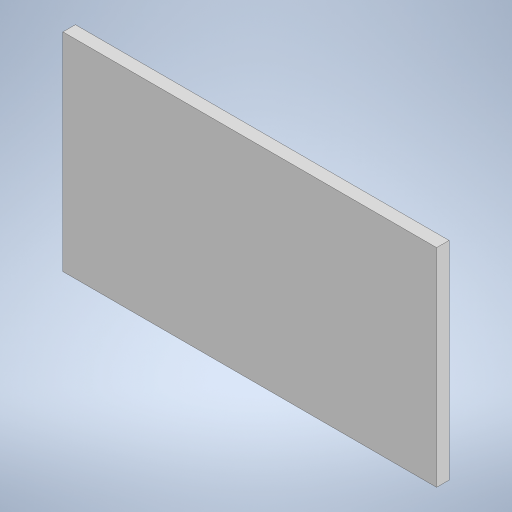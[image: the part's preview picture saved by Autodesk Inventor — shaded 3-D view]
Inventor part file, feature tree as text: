
AUTODESK INVENTOR PART (.ipt)
format: ipt  version: 2023 (Build 270158000, 158)  size: 182,784 bytes
history: native  units: mm
features: other x1, extrude x1, sketch x1
ambient origin geometry x8: Origin, YZ Plane, XZ Plane, XY Plane, X Axis, Y Axis, Z Axis, Center Point
bodies: Body1 (feature_tree)
feature tree (3):
  other  "ソリッド1"
  extrude  "押し出し1"  Depth=90.0mm
  sketch  "スケッチ1"
